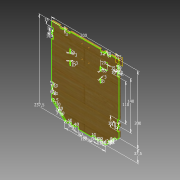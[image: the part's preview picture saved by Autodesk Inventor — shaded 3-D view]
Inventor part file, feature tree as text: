
AUTODESK INVENTOR PART (.ipt)
format: ipt  version: 2014 (Build 180170000, 170)  size: 346,624 bytes
history: native  units: mm
features: sketch x3, extrude x3, plane x2
ambient origin geometry x8: Origin, YZ Plane, XZ Plane, XY Plane, X Axis, Y Axis, Z Axis, Center Point
bodies: Body1 (feature_tree)
feature tree (8):
  sketch  "Sketch1"  dims[d41=2.5mm d326=10.0mm]
  plane  "Work Plane2"
  sketch  "Sketch2"  dims[d327=10.0mm d328=10.0mm]
  plane  "Work Plane1"
  sketch  "Sketch3"  dims[d329=5.0mm d330=5.0mm d381=5.0mm d382=10.0mm d383=10.0mm d384=5.0mm d385=10.0mm d392=5.0mm d393=10.0mm d458=35.0mm d460=20.0mm d465=10.0mm d466=3.0mm d467=10.0mm d468=3.0mm d469=10.0mm d470=3.0mm d471=10.0mm d472=3.0mm d475=40.0mm d476=5.0mm d477=5.0mm d489=3.0mm d512=3.0mm d513=3.0mm d514=3.0mm d515=3.0mm d529=15.0mm d530=10.0mm d531=5.0mm d532=5.0mm d533=10.0mm d535=200.0mm d539=37.5mm d543=2.5mm d558=5.0mm d573=10.0mm d574=140.0mm d575=110.0mm d576=30.0mm d580=15.0mm d581=3.0mm d583=5.0mm d584=10.0mm d586=5.0mm d587=10.0mm d594=120.0mm d595=10.0mm d596=5.0mm d597=10.0mm d598=10.0mm d599=10.0mm d600=3.0mm d602=5.0mm d603=10.0mm d604=10.0mm d605=10.0mm d606=3.0mm d607=5.0mm d608=0.0mm d609=5.0mm d610=0.0mm d611=40.0mm d612=25.0mm d613=70.0mm d636=200.0mm d637=37.5mm d638=237.5mm d653=5.0mm d654=10.0mm d655=10.0mm d656=10.0mm d657=5.0mm d658=2.5mm d659=3.0mm d662=5.0mm d663=90.0deg d664=10.0mm d665=10.0mm d666=10.0mm d667=5.0mm d668=2.5mm d669=3.0mm d674=5.0mm d676=12.5mm d677=5.0mm d678=0.0mm]
  extrude  "Extrusion37"  Depth=10.0mm
  extrude  "Extrusion38"  Depth=10.0mm
  extrude  "Extrusion42"  Depth=5.0mm
